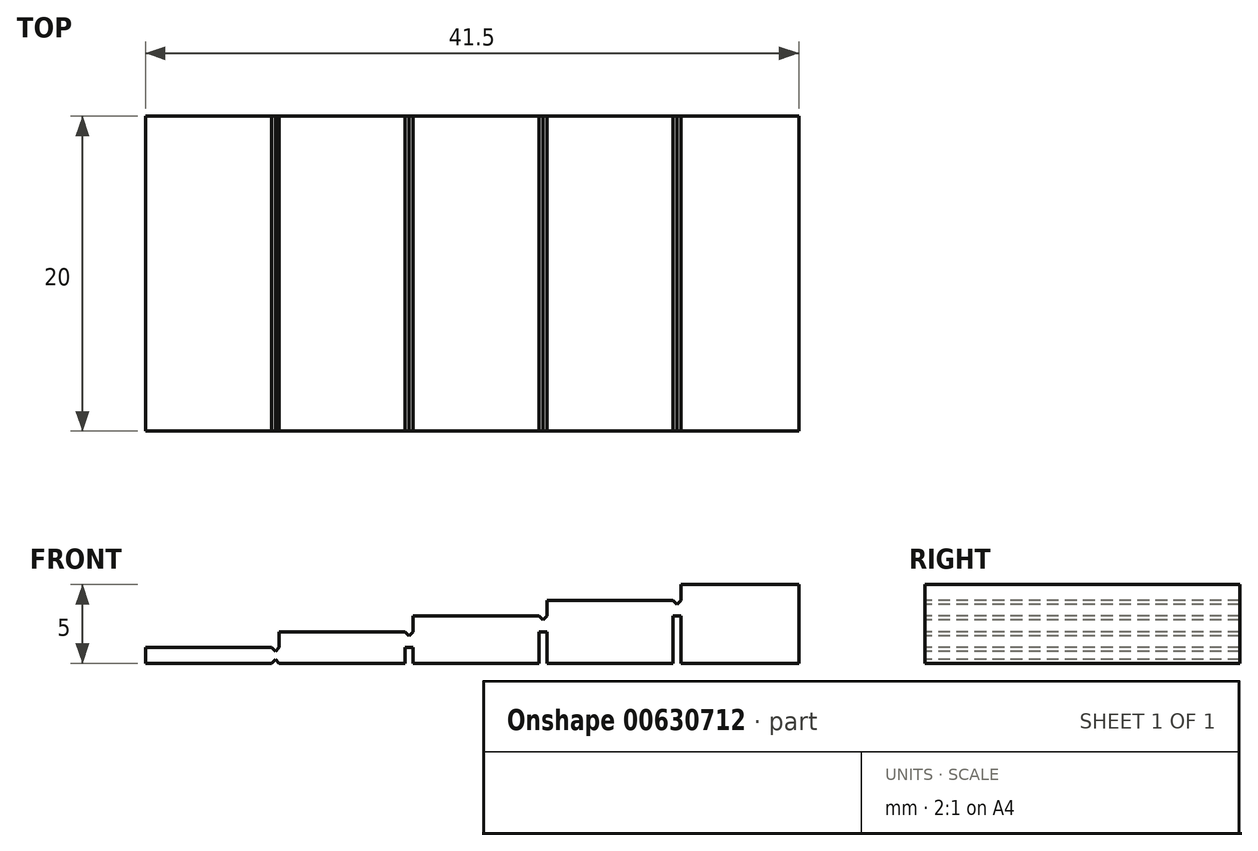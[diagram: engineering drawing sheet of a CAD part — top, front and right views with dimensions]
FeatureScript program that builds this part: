
annotation { "Feature Type Name" : "Feature", "Feature Type Description" : "" }
export const myFeature = defineFeature(function(context is Context, id is Id, definition is map)
    precondition{}
    {
        {
            var Q0;
            Q0=qCreatedBy(makeId("Top.planeOp"),FACE);
            var sketch = newSketch(context, id + "F0", { "sketchPlane" : qUnion([Q0])});
            skLineSegment(sketch, "E0.bottom", {"start": v(0, 0) * mm, "end": v(50, 0) * mm});
            skLineSegment(sketch, "E0.top", {"start": v(0, 20) * mm, "end": v(50, 20) * mm});
            skLineSegment(sketch, "E0.left", {"start": v(0, 0) * mm, "end": v(0, 20) * mm});
            skLineSegment(sketch, "E0.right", {"start": v(50, 0) * mm, "end": v(50, 20) * mm});
            skSolve(sketch);
        }
        {
            var Q0;
            Q0 = qSketchRegion(id + "F0", true);
            extrude(context, id + "F1", {"entities" : qUnion([Q0]), "depth" : 5 * mm, "offsetDistance" : 25 * mm});
        }
        {
            var Q0;
            Q0=makeQuery(id+"F1.opExtrude","SWEPT_FACE",FACE,{"disambiguationData":[OSD([sQuery(id+"F0.wireOp",EDGE,"E0.bottom")])]});
            var sketch = newSketch(context, id + "F2", { "sketchPlane" : qUnion([Q0])});
            skLineSegment(sketch, "E1", {"start": v(0, 0) * mm, "end": v(42.5, 5) * mm});
            skSolve(sketch);
        }
        {
            var Q0;
            {var subQ0=sQuery(id+"F2.wireOp",EDGE,"E1");Q0=makeQuery(id+"F2.imprint","IMPRINT",FACE,{"disambiguationData":[TD([[makeQuery(id+"F2.imprint","IMPRINT",EDGE,{"derivedFrom":subQ0}),1.0]])]});}
            extrude(context, id + "F3", {"entities" : qUnion([Q0]), "operationType" : NewBodyOperationType.REMOVE, "oppositeDirection" : true, "depth" : 25 * mm, "offsetDistance" : 25 * mm});
        }
        {
            var Q0;
            Q0=makeQuery(id+"F1.opExtrude","SWEPT_FACE",FACE,{"disambiguationData":[OSD([sQuery(id+"F0.wireOp",EDGE,"E0.bottom")])]});
            var sketch = newSketch(context, id + "F4", { "sketchPlane" : qUnion([Q0])});
            skLineSegment(sketch, "E2", {"start": v(-11.86, 1) * mm, "end": v(68.27, 1) * mm, "construction": true});
            skLineSegment(sketch, "E3", {"start": v(-11.86, 2) * mm, "end": v(68.02, 2) * mm, "construction": true});
            skLineSegment(sketch, "E4", {"start": v(68.02, 3) * mm, "end": v(-12.78, 3) * mm, "construction": true});
            skLineSegment(sketch, "E5", {"start": v(-12.78, 4) * mm, "end": v(63.89, 4) * mm, "construction": true});
            skLineSegment(sketch, "E6", {"start": v(64.5, 5) * mm, "end": v(5.43, 5) * mm, "construction": true});
            skLineSegment(sketch, "E7", {"start": v(6.97, 6) * mm, "end": v(55.18, 6) * mm, "construction": true});
            skLineSegment(sketch, "E8", {"start": v(55.18, 7) * mm, "end": v(16.91, 7) * mm, "construction": true});
            skLineSegment(sketch, "E9", {"start": v(16.9, 5) * mm, "end": v(64.05, 5) * mm, "construction": true});
            skLineSegment(sketch, "E10", {"start": v(63.45, 8) * mm, "end": v(25.8, 8) * mm, "construction": true});
            skLineSegment(sketch, "E11", {"start": v(26.51, 9) * mm, "end": v(70.06, 9) * mm, "construction": true});
            skLineSegment(sketch, "E12.0", {"start": v(0, 0) * mm, "end": v(42.5, 5) * mm});
            skLineSegment(sketch, "E13", {"start": v(17, 2) * mm, "end": v(17, 1) * mm});
            skLineSegment(sketch, "E14", {"start": v(17, 1) * mm, "end": v(8.5, 1) * mm});
            skLineSegment(sketch, "E15", {"start": v(17, 2) * mm, "end": v(25.5, 2) * mm});
            skLineSegment(sketch, "E16", {"start": v(25.5, 2) * mm, "end": v(25.5, 3) * mm});
            skLineSegment(sketch, "E17", {"start": v(25.5, 3) * mm, "end": v(34, 3) * mm});
            skLineSegment(sketch, "E18", {"start": v(34, 3) * mm, "end": v(34, 4) * mm});
            skLineSegment(sketch, "E19", {"start": v(34, 4) * mm, "end": v(42.5, 4) * mm});
            skLineSegment(sketch, "E20", {"start": v(42.5, 4) * mm, "end": v(42.5, 5) * mm});
            skLineSegment(sketch, "E21", {"start": v(17, 1) * mm, "end": v(16.75, 0.75) * mm});
            skLineSegment(sketch, "E22", {"start": v(16.75, 0.75) * mm, "end": v(16.5, 1) * mm});
            skLineSegment(sketch, "E23", {"start": v(16.5, 1) * mm, "end": v(17, 1) * mm});
            skLineSegment(sketch, "E24", {"start": v(13.02, 0.5) * mm, "end": v(19.55, 0.5) * mm, "construction": true});
            skLineSegment(sketch, "E25.MirrorCS", {"start": v(16.75, 0.25) * mm, "end": v(16.5, 0) * mm});
            skLineSegment(sketch, "E26.MirrorCS", {"start": v(16.5, 0) * mm, "end": v(17, 0) * mm});
            skLineSegment(sketch, "E27.MirrorCS", {"start": v(17, 0) * mm, "end": v(16.75, 0.25) * mm});
            skLineSegment(sketch, "E28", {"start": v(25.5, 2) * mm, "end": v(25.25, 1.75) * mm});
            skLineSegment(sketch, "E29", {"start": v(25.25, 1.75) * mm, "end": v(25, 2) * mm});
            skLineSegment(sketch, "E30", {"start": v(25, 2) * mm, "end": v(25.5, 2) * mm});
            skLineSegment(sketch, "E31", {"start": v(34, 3) * mm, "end": v(33.75, 2.75) * mm});
            skLineSegment(sketch, "E32", {"start": v(33.75, 2.75) * mm, "end": v(33.5, 3) * mm});
            skLineSegment(sketch, "E33", {"start": v(33.5, 3) * mm, "end": v(34, 3) * mm});
            skLineSegment(sketch, "E34", {"start": v(42.5, 4) * mm, "end": v(42.25, 3.75) * mm});
            skLineSegment(sketch, "E35", {"start": v(42.25, 3.75) * mm, "end": v(42, 4) * mm});
            skLineSegment(sketch, "E36", {"start": v(42, 4) * mm, "end": v(42.5, 4) * mm});
            skLineSegment(sketch, "E37.bottom", {"start": v(42.5, 0) * mm, "end": v(42.02, 0) * mm});
            skLineSegment(sketch, "E37.top", {"start": v(42.5, 3) * mm, "end": v(42.02, 3) * mm});
            skLineSegment(sketch, "E37.left", {"start": v(42.5, 0) * mm, "end": v(42.5, 3) * mm});
            skLineSegment(sketch, "E37.right", {"start": v(42.02, 0) * mm, "end": v(42.02, 3) * mm});
            skLineSegment(sketch, "E38.bottom", {"start": v(34, 0) * mm, "end": v(33.5, 0) * mm});
            skLineSegment(sketch, "E38.top", {"start": v(34, 2) * mm, "end": v(33.5, 2) * mm});
            skLineSegment(sketch, "E38.left", {"start": v(34, 0) * mm, "end": v(34, 2) * mm});
            skLineSegment(sketch, "E38.right", {"start": v(33.5, 0) * mm, "end": v(33.5, 2) * mm});
            skPoint(sketch, "E39.firstSnap0", {"position": v(25, 0) * mm});
            skPoint(sketch, "E39.oppositeSnap0", {"position": v(25, 0) * mm});
            skLineSegment(sketch, "E39.bottom", {"start": v(25.5, 0) * mm, "end": v(25, 0) * mm});
            skLineSegment(sketch, "E39.top", {"start": v(25.5, 1) * mm, "end": v(25, 1) * mm});
            skLineSegment(sketch, "E39.left", {"start": v(25.5, 0) * mm, "end": v(25.5, 1) * mm});
            skLineSegment(sketch, "E39.right", {"start": v(25, 0) * mm, "end": v(25, 1) * mm});
            skSolve(sketch);
        }
        {
            var Q0;
            Q0 = qSketchRegion(id + "F4", true);
            extrude(context, id + "F5", {"entities" : qUnion([Q0]), "operationType" : NewBodyOperationType.REMOVE, "oppositeDirection" : true, "depth" : 25 * mm, "offsetDistance" : 25 * mm});
        }
        {
            var Q0;
            Q0=makeQuery(id+"F1.opExtrude","SWEPT_FACE",FACE,{"disambiguationData":[OSD([sQuery(id+"F0.wireOp",EDGE,"E0.bottom")])]});
            var sketch = newSketch(context, id + "F6", { "sketchPlane" : qUnion([Q0])});
            skLineSegment(sketch, "E40", {"start": v(8.5, 1) * mm, "end": v(8.5, 0) * mm});
            skPoint(sketch, "E40.endSnap0", {"position": v(8.25, 0) * mm});
            skSolve(sketch);
        }
        {
            var Q0;
            Q0 = qSketchRegion(id + "F6", true);
            var Q1;
            {var subQ0=sQuery(id+"F6.wireOp",EDGE,"E40");Q1=makeQuery(id+"F6.imprint","IMPRINT",FACE,{"disambiguationData":[TD([[makeQuery(id+"F6.imprint","IMPRINT",EDGE,{"derivedFrom":subQ0}),-1.0]])]});}
            extrude(context, id + "F7", {"entities" : qUnion([Q0, Q1]), "operationType" : NewBodyOperationType.REMOVE, "oppositeDirection" : true, "depth" : 25 * mm, "offsetDistance" : 25 * mm});
        }
    });
